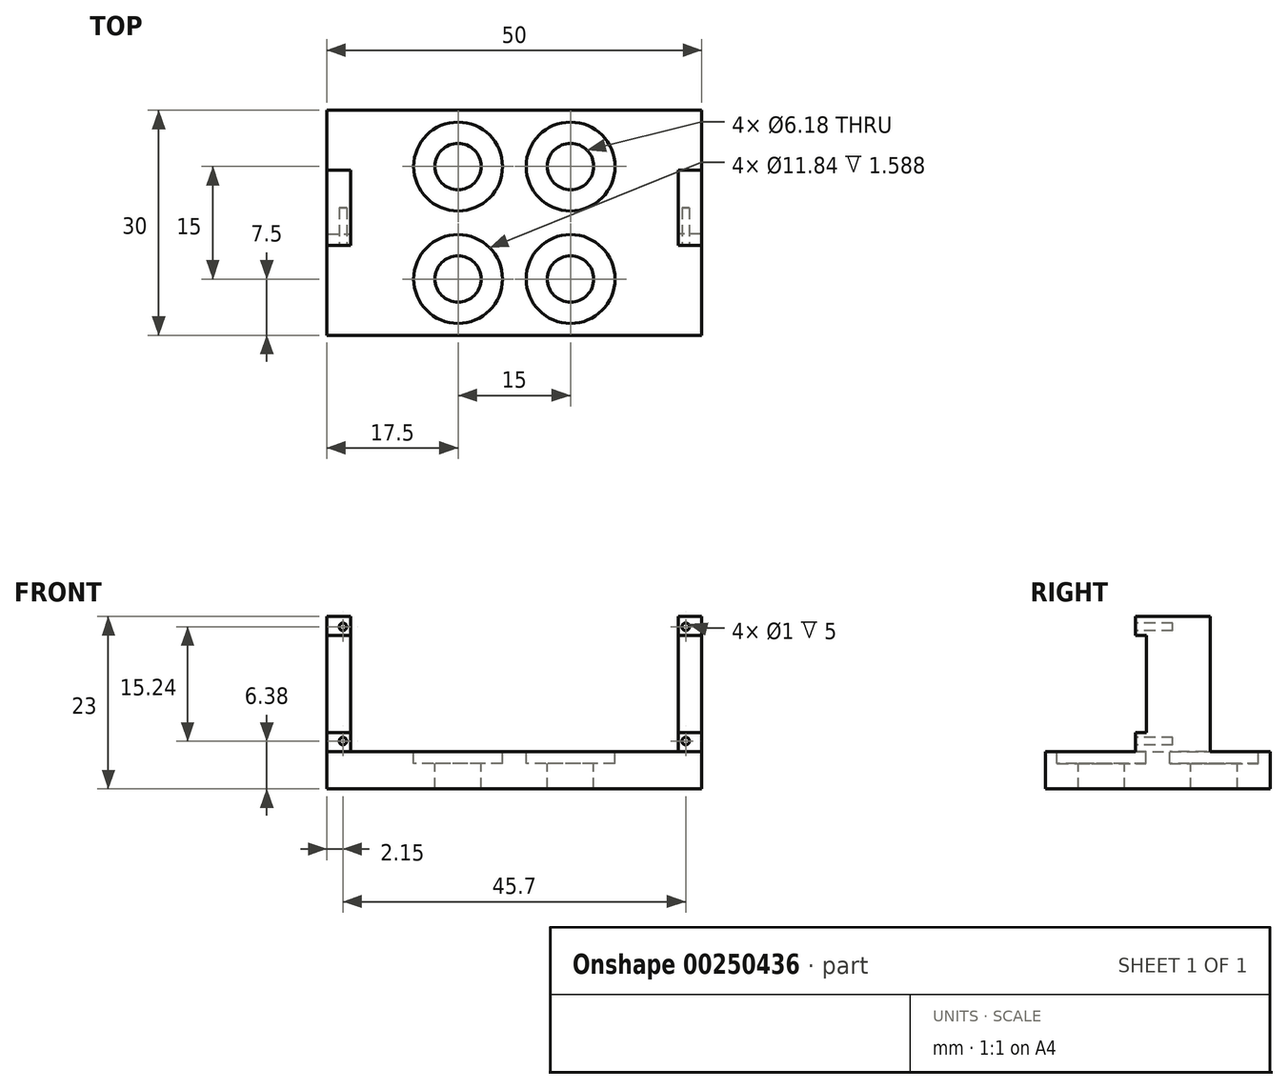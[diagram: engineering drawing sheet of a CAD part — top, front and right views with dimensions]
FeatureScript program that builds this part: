
annotation { "Feature Type Name" : "Feature", "Feature Type Description" : "" }
export const myFeature = defineFeature(function(context is Context, id is Id, definition is map)
    precondition{}
    {
        {
            var Q0;
            Q0=qCreatedBy(makeId("Top.planeOp"),FACE);
            var sketch = newSketch(context, id + "F0", { "sketchPlane" : qUnion([Q0])});
            skLineSegment(sketch, "E0.bottom", {"start": v(-25, 15) * mm, "end": v(25, 15) * mm});
            skLineSegment(sketch, "E0.top", {"start": v(-25, -15) * mm, "end": v(25, -15) * mm});
            skLineSegment(sketch, "E0.left", {"start": v(-25, 15) * mm, "end": v(-25, -15) * mm});
            skLineSegment(sketch, "E0.right", {"start": v(25, 15) * mm, "end": v(25, -15) * mm});
            skSolve(sketch);
        }
        {
            var Q0;
            Q0=makeQuery(id+"F0.imprint","IMPRINT",FACE,{"disambiguationData":[TD([[makeQuery(id+"F0.imprint","IMPRINT",EDGE,{"derivedFrom":sQuery(id+"F0.wireOp",EDGE,"E0.bottom")}),-1.0]])]});
            extrude(context, id + "F1", {"entities" : qUnion([Q0]), "depth" : 5 * mm});
        }
        {
            var Q0;
            Q0=makeQuery(id+"F1.opExtrude","CAP_FACE",FACE,{"disambiguationData":[OSD([sQuery(id+"F0.wireOp",EDGE,"E0.bottom"),sQuery(id+"F0.wireOp",EDGE,"E0.top"),sQuery(id+"F0.wireOp",EDGE,"E0.left"),sQuery(id+"F0.wireOp",EDGE,"E0.right")])],"isStart":false});
            var sketch = newSketch(context, id + "F2", { "sketchPlane" : qUnion([Q0])});
            skLineSegment(sketch, "E1.bottom", {"start": v(-7.5, 7.5) * mm, "end": v(7.5, 7.5) * mm, "construction": true});
            skLineSegment(sketch, "E1.top", {"start": v(-7.5, -7.5) * mm, "end": v(7.5, -7.5) * mm, "construction": true});
            skLineSegment(sketch, "E1.left", {"start": v(-7.5, 7.5) * mm, "end": v(-7.5, -7.5) * mm, "construction": true});
            skLineSegment(sketch, "E1.right", {"start": v(7.5, 7.5) * mm, "end": v(7.5, -7.5) * mm, "construction": true});
            skCircle(sketch, "E2", {"center": v(-7.5, 7.5) * mm, "radius": 3.09 * mm});
            skCircle(sketch, "E3", {"center": v(7.5, 7.5) * mm, "radius": 3.09 * mm});
            skCircle(sketch, "E4", {"center": v(7.5, -7.5) * mm, "radius": 3.09 * mm});
            skCircle(sketch, "E5", {"center": v(-7.5, -7.5) * mm, "radius": 3.09 * mm});
            skSolve(sketch);
        }
        {
            var Q0;
            Q0 = qSketchRegion(id + "F2", true);
            extrude(context, id + "F3", {"entities" : qUnion([Q0]), "operationType" : NewBodyOperationType.REMOVE, "endBound" : BoundingType.THROUGH_ALL, "oppositeDirection" : true, "depth" : 25 * mm});
        }
        {
            var Q0;
            Q0=makeQuery(id+"F1.opExtrude","CAP_FACE",FACE,{"disambiguationData":[OSD([sQuery(id+"F0.wireOp",EDGE,"E0.bottom"),sQuery(id+"F0.wireOp",EDGE,"E0.top"),sQuery(id+"F0.wireOp",EDGE,"E0.left"),sQuery(id+"F0.wireOp",EDGE,"E0.right")])],"isStart":false});
            var sketch = newSketch(context, id + "F4", { "sketchPlane" : qUnion([Q0])});
            skCircle(sketch, "E6", {"center": v(-7.5, 7.5) * mm, "radius": 5.92 * mm});
            skCircle(sketch, "E7", {"center": v(7.5, 7.5) * mm, "radius": 5.92 * mm});
            skCircle(sketch, "E8", {"center": v(-7.5, -7.5) * mm, "radius": 5.92 * mm});
            skCircle(sketch, "E9", {"center": v(7.5, -7.5) * mm, "radius": 5.92 * mm});
            skSolve(sketch);
        }
        {
            var Q0;
            Q0 = qSketchRegion(id + "F4", true);
            extrude(context, id + "F5", {"entities" : qUnion([Q0]), "operationType" : NewBodyOperationType.REMOVE, "oppositeDirection" : true, "depth" : 1.59 * mm});
        }
        {
            var Q0;
            Q0=qCreatedBy(makeId("Front.planeOp"),FACE);
            var sketch = newSketch(context, id + "F6", { "sketchPlane" : qUnion([Q0])});
            skLineSegment(sketch, "E10.0", {"start": v(-25, 5) * mm, "end": v(-21.85, 5) * mm});
            skLineSegment(sketch, "E11", {"start": v(-25, 5) * mm, "end": v(-25, 23) * mm});
            skLineSegment(sketch, "E12", {"start": v(-25, 23) * mm, "end": v(-21.85, 23) * mm});
            skLineSegment(sketch, "E13", {"start": v(-21.85, 23) * mm, "end": v(-21.85, 5) * mm});
            skLineSegment(sketch, "E14.MirrorCS", {"start": v(25, 5) * mm, "end": v(25, 23) * mm});
            skLineSegment(sketch, "E15.MirrorCS", {"start": v(25, 23) * mm, "end": v(21.85, 23) * mm});
            skLineSegment(sketch, "E16.MirrorCS", {"start": v(21.85, 23) * mm, "end": v(21.85, 5) * mm});
            skLineSegment(sketch, "E17.trimOffspring", {"start": v(21.85, 5) * mm, "end": v(25, 5) * mm});
            skSolve(sketch);
        }
        {
            var Q0;
            Q0 = qSketchRegion(id + "F6", true);
            extrude(context, id + "F7", {"entities" : qUnion([Q0]), "operationType" : NewBodyOperationType.ADD, "depth" : 1.5 * mm});
        }
        {
            var Q0;
            Q0=makeQuery(id+"F7.opExtrude","CAP_FACE",FACE,{"disambiguationData":[OSD([sQuery(id+"F6.wireOp",EDGE,"E10.0"),sQuery(id+"F6.wireOp",EDGE,"E11"),sQuery(id+"F6.wireOp",EDGE,"E12"),sQuery(id+"F6.wireOp",EDGE,"E13")])],"isStart":false});
            var sketch = newSketch(context, id + "F8", { "sketchPlane" : qUnion([Q0])});
            skLineSegment(sketch, "E18.0", {"start": v(-25, 23) * mm, "end": v(-21.85, 23) * mm});
            skLineSegment(sketch, "E19.0", {"start": v(-25, 5) * mm, "end": v(-21.85, 5) * mm});
            skLineSegment(sketch, "E20.0", {"start": v(-25, 5) * mm, "end": v(-25, 7.5) * mm});
            skLineSegment(sketch, "E21.0", {"start": v(-21.85, 23) * mm, "end": v(-21.85, 20.5) * mm});
            skLineSegment(sketch, "E22", {"start": v(-25, 20.5) * mm, "end": v(-21.85, 20.5) * mm});
            skLineSegment(sketch, "E23", {"start": v(-25, 7.5) * mm, "end": v(-21.85, 7.5) * mm});
            skLineSegment(sketch, "E24.trimOffspring", {"start": v(-21.85, 7.5) * mm, "end": v(-21.85, 5) * mm});
            skLineSegment(sketch, "E25.trimOffspring", {"start": v(-25, 20.5) * mm, "end": v(-25, 23) * mm});
            skPoint(sketch, "E26.orphan", {"position": v(25, 5) * mm});
            skLineSegment(sketch, "E27.MirrorCS", {"start": v(25, 20.5) * mm, "end": v(25, 23) * mm});
            skLineSegment(sketch, "E28.MirrorCS", {"start": v(21.85, 7.5) * mm, "end": v(21.85, 5) * mm});
            skLineSegment(sketch, "E29.MirrorCS", {"start": v(25, 5) * mm, "end": v(25, 7.5) * mm});
            skLineSegment(sketch, "E30.MirrorCS", {"start": v(21.85, 23) * mm, "end": v(21.85, 20.5) * mm});
            skLineSegment(sketch, "E31.MirrorCS", {"start": v(25, 20.5) * mm, "end": v(21.85, 20.5) * mm});
            skLineSegment(sketch, "E32.MirrorCS", {"start": v(25, 5) * mm, "end": v(21.85, 5) * mm});
            skLineSegment(sketch, "E33.MirrorCS", {"start": v(25, 7.5) * mm, "end": v(21.85, 7.5) * mm});
            skLineSegment(sketch, "E34.MirrorCS", {"start": v(25, 23) * mm, "end": v(21.85, 23) * mm});
            skSolve(sketch);
        }
        {
            var Q0;
            Q0 = qSketchRegion(id + "F8", true);
            extrude(context, id + "F9", {"entities" : qUnion([Q0]), "operationType" : NewBodyOperationType.ADD, "depth" : 1.5 * mm});
        }
        {
            var Q0;
            Q0=makeQuery(id+"F7.opExtrude","CAP_FACE",FACE,{"disambiguationData":[OSD([sQuery(id+"F6.wireOp",EDGE,"E14.MirrorCS"),sQuery(id+"F6.wireOp",EDGE,"E15.MirrorCS"),sQuery(id+"F6.wireOp",EDGE,"E16.MirrorCS"),sQuery(id+"F6.wireOp",EDGE,"E17.trimOffspring")])],"isStart":true});
            var Q1;
            Q1=makeQuery(id+"F7.opExtrude","CAP_FACE",FACE,{"disambiguationData":[OSD([sQuery(id+"F6.wireOp",EDGE,"E10.0"),sQuery(id+"F6.wireOp",EDGE,"E11"),sQuery(id+"F6.wireOp",EDGE,"E12"),sQuery(id+"F6.wireOp",EDGE,"E13")])],"isStart":true});
            var Q2;
            Q2=makeQuery(id+"F1.opExtrude","SWEPT_FACE",FACE,{"disambiguationData":[OSD([sQuery(id+"F0.wireOp",EDGE,"E0.bottom")])]});
            extrude(context, id + "F10", {"entities" : qUnion([Q0, Q1]), "operationType" : NewBodyOperationType.ADD, "endBoundEntityFace" : qUnion([Q2]), "depth" : 7 * mm});
        }
        {
            var Q0;
            Q0=makeQuery(id+"F9.opExtrude","CAP_FACE",FACE,{"disambiguationData":[OSD([sQuery(id+"F8.wireOp",EDGE,"E18.0"),sQuery(id+"F8.wireOp",EDGE,"E21.0"),sQuery(id+"F8.wireOp",EDGE,"E22"),sQuery(id+"F8.wireOp",EDGE,"E25.trimOffspring")])],"isStart":false});
            var sketch = newSketch(context, id + "F11", { "sketchPlane" : qUnion([Q0])});
            skCircle(sketch, "E35", {"center": v(-22.85, 6.38) * mm, "radius": 0.5 * mm});
            skCircle(sketch, "E36", {"center": v(-22.85, 21.62) * mm, "radius": 0.5 * mm});
            skCircle(sketch, "E37.MirrorC", {"center": v(22.85, 21.62) * mm, "radius": 0.5 * mm});
            skCircle(sketch, "E38.MirrorC", {"center": v(22.85, 6.38) * mm, "radius": 0.5 * mm});
            skSolve(sketch);
        }
        {
            var Q0;
            Q0 = qSketchRegion(id + "F11", true);
            extrude(context, id + "F12", {"entities" : qUnion([Q0]), "operationType" : NewBodyOperationType.REMOVE, "oppositeDirection" : true, "depth" : 5 * mm});
        }
    });
